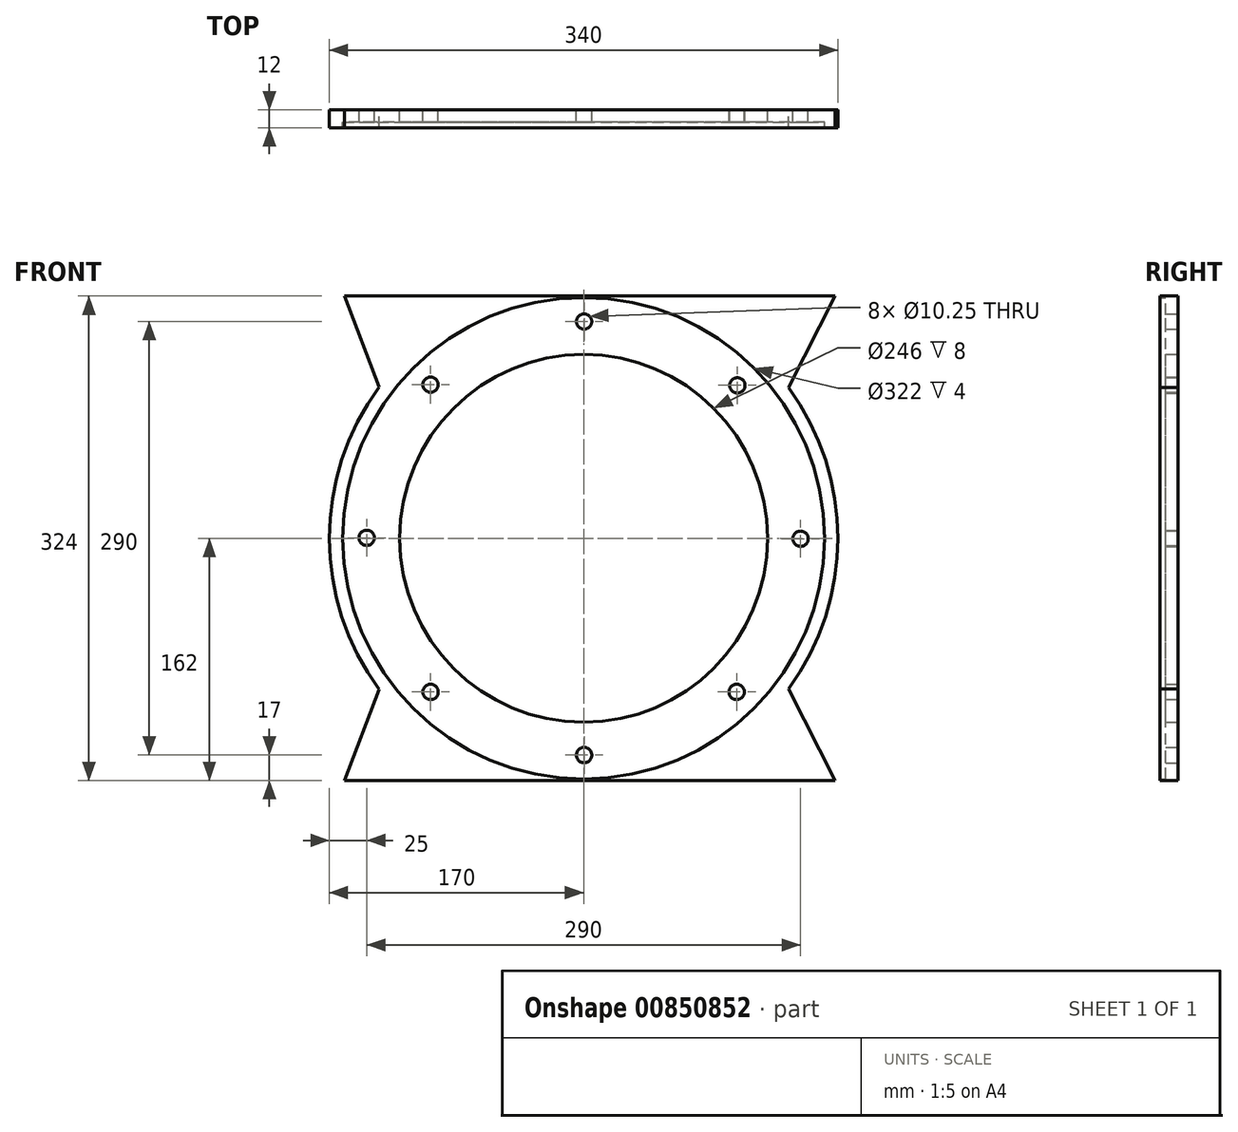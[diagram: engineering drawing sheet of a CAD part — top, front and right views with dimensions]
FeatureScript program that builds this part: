
annotation { "Feature Type Name" : "Feature", "Feature Type Description" : "" }
export const myFeature = defineFeature(function(context is Context, id is Id, definition is map)
    precondition{}
    {
        {
            var Q0;
            Q0=qCreatedBy(makeId("Front.planeOp"),FACE);
            var sketch = newSketch(context, id + "F0", { "sketchPlane" : qUnion([Q0])});
            skLineSegment(sketch, "E0", {"start": v(-463.43, 162) * mm, "end": v(-135.53, 162) * mm});
            skLineSegment(sketch, "E1", {"start": v(-135.52, -162) * mm, "end": v(-463.43, -162) * mm});
            skCircle(sketch, "E2", {"center": v(-303.63, 0) * mm, "radius": 161 * mm});
            skCircle(sketch, "E3", {"center": v(-303.63, 0) * mm, "radius": 123 * mm});
            skCircle(sketch, "E4", {"center": v(-303.32, 145) * mm, "radius": 5.13 * mm});
            skCircle(sketch, "E5", {"center": v(-303.32, -145) * mm, "radius": 5.13 * mm});
            skCircle(sketch, "E6", {"center": v(-158.63, -0.3) * mm, "radius": 5.13 * mm});
            skCircle(sketch, "E7", {"center": v(-448.63, 0.32) * mm, "radius": 5.13 * mm});
            skCircle(sketch, "E8", {"center": v(-405.93, 102.76) * mm, "radius": 5.13 * mm});
            skCircle(sketch, "E9", {"center": v(-200.87, 102.3) * mm, "radius": 5.13 * mm});
            skCircle(sketch, "E10", {"center": v(-405.94, -102.75) * mm, "radius": 5.13 * mm});
            skCircle(sketch, "E11", {"center": v(-201.32, -102.75) * mm, "radius": 5.13 * mm});
            skLineSegment(sketch, "E12", {"start": v(-135.53, 162) * mm, "end": v(-166.8, 100.87) * mm});
            skLineSegment(sketch, "E13", {"start": v(-440.25, 101.17) * mm, "end": v(-463.43, 162) * mm});
            skLineSegment(sketch, "E14", {"start": v(-440.25, -101.17) * mm, "end": v(-463.43, -162) * mm});
            skArc(sketch, "E15", {"start": v(-440.25, 101.17) * mm, "mid": v(-473.63, 0) * mm, "end": v(-440.25, -101.17) * mm});
            skArc(sketch, "E16", {"start": v(-166.8, 100.87) * mm, "mid": v(-133.63, 0) * mm, "end": v(-166.79, -100.87) * mm});
            skLineSegment(sketch, "E17", {"start": v(-166.79, -100.87) * mm, "end": v(-135.52, -162) * mm});
            skSolve(sketch);
        }
        {
            var Q0;
            Q0=makeQuery(id+"F0.imprint","IMPRINT",FACE,{"disambiguationData":[TD([[makeQuery(id+"F0.imprint","IMPRINT",EDGE,{"derivedFrom":sQuery(id+"F0.wireOp",EDGE,"E2")}),1.0]])]});
            extrude(context, id + "F1", {"entities" : qUnion([Q0]), "depth" : 8 * mm, "offsetDistance" : 25.4 * mm});
        }
        {
            var Q0;
            Q0=makeQuery(id+"F0.imprint","IMPRINT",FACE,{"disambiguationData":[TD([[makeQuery(id+"F0.imprint","IMPRINT",EDGE,{"derivedFrom":sQuery(id+"F0.wireOp",EDGE,"E0")}),-1.0]])]});
            extrude(context, id + "F2", {"entities" : qUnion([Q0]), "operationType" : NewBodyOperationType.ADD, "depth" : 12 * mm, "offsetDistance" : 25.4 * mm});
        }
    });
